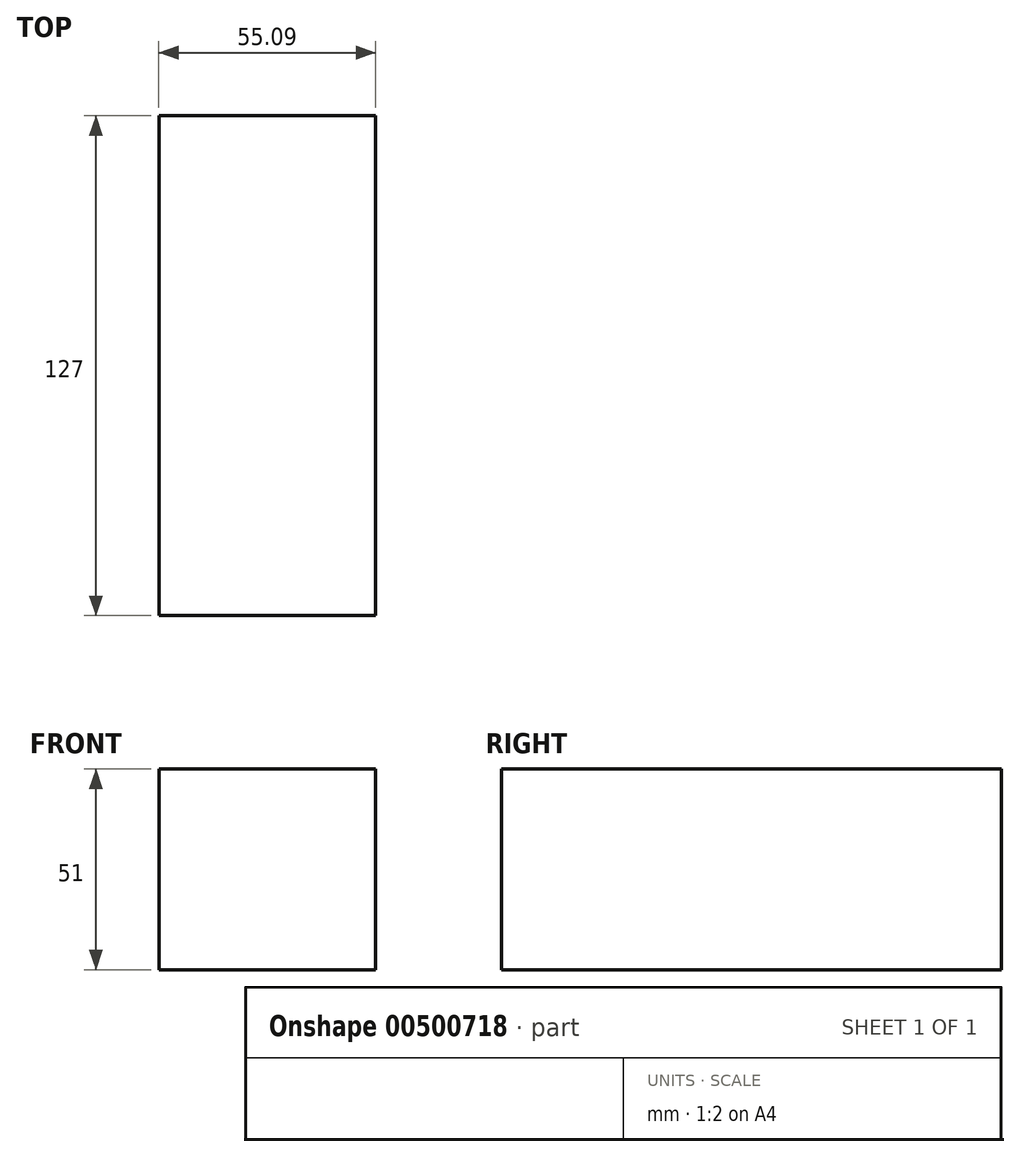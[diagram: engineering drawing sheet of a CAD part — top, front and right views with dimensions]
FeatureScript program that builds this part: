
annotation { "Feature Type Name" : "Feature", "Feature Type Description" : "" }
export const myFeature = defineFeature(function(context is Context, id is Id, definition is map)
    precondition{}
    {
        {
            var Q0;
            Q0=qCreatedBy(makeId("Front.planeOp"),FACE);
            var sketch = newSketch(context, id + "F0", { "sketchPlane" : qUnion([Q0])});
            skLineSegment(sketch, "E0.bottom", {"start": v(-20.99, 25.5) * mm, "end": v(34.1, 25.5) * mm});
            skLineSegment(sketch, "E0.top", {"start": v(-20.99, -25.5) * mm, "end": v(34.1, -25.5) * mm});
            skLineSegment(sketch, "E0.left", {"start": v(-20.99, 25.5) * mm, "end": v(-20.99, -25.5) * mm});
            skLineSegment(sketch, "E0.right", {"start": v(34.1, 25.5) * mm, "end": v(34.1, -25.5) * mm});
            skSolve(sketch);
        }
        {
            var Q0;
            Q0=makeQuery(id+"F0.imprint","IMPRINT",FACE,{"disambiguationData":[TD([[makeQuery(id+"F0.imprint","IMPRINT",EDGE,{"derivedFrom":sQuery(id+"F0.wireOp",EDGE,"E0.bottom")}),-1.0]])]});
            extrude(context, id + "F1", {"entities" : qUnion([Q0]), "depth" : 127 * mm});
        }
    });
